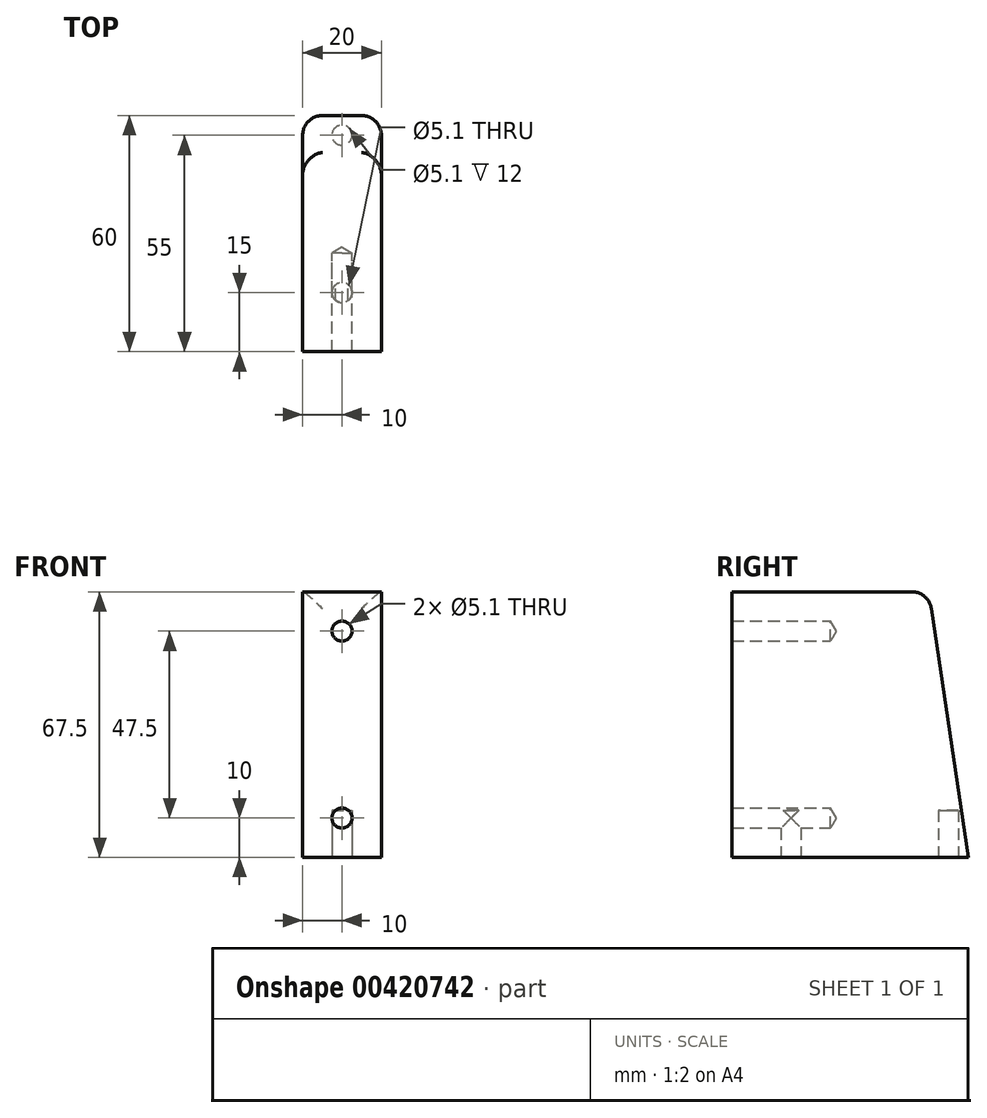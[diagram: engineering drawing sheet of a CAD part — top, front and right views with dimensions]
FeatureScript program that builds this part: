
annotation { "Feature Type Name" : "Feature", "Feature Type Description" : "" }
export const myFeature = defineFeature(function(context is Context, id is Id, definition is map)
    precondition{}
    {
        {
            var Q0;
            Q0=qCreatedBy(makeId("Right.planeOp"),FACE);
            var sketch = newSketch(context, id + "F0", { "sketchPlane" : qUnion([Q0])});
            skLineSegment(sketch, "E0", {"start": v(0, 0) * mm, "end": v(-60, 0) * mm});
            skLineSegment(sketch, "E1", {"start": v(-60, 0) * mm, "end": v(-60, 67.5) * mm});
            skLineSegment(sketch, "E2", {"start": v(-60, 67.5) * mm, "end": v(-10, 67.5) * mm});
            skLineSegment(sketch, "E3", {"start": v(-10, 67.5) * mm, "end": v(0, 0) * mm});
            skSolve(sketch);
        }
        {
            var Q0;
            Q0=qSketchRegion(id+"F0",true);
            extrude(context, id + "F1", {"entities" : qUnion([Q0]), "depth" : 20 * mm});
        }
        {
            var Q0;
            Q0=makeQuery(id+"F1.opExtrude","SWEPT_FACE",FACE,{"disambiguationData":[OSD([sQuery(id+"F0.wireOp",EDGE,"E1")])]});
            var sketch = newSketch(context, id + "F2", { "sketchPlane" : qUnion([Q0])});
            skLineSegment(sketch, "E4", {"start": v(10, 67.5) * mm, "end": v(10, 57.5) * mm});
            skLineSegment(sketch, "E5", {"start": v(10, 0) * mm, "end": v(10, 10) * mm});
            skSolve(sketch);
        }
        {
            var Q0;
            Q0=sQuery(id+"F2.wireOp",VERTEX,"E4.end");
            var Q1;
            Q1=sQuery(id+"F2.wireOp",VERTEX,"E5.end");
            var Q2;
            Q2=makeQuery(id+"F1.opExtrude","SWEPT_BODY",BODY,{"disambiguationData":[OSD([sQuery(id+"F0.wireOp",EDGE,"E0"),sQuery(id+"F0.wireOp",EDGE,"E1"),sQuery(id+"F0.wireOp",EDGE,"E2"),sQuery(id+"F0.wireOp",EDGE,"E3")])]});
            hole(context, id + "F3", {"style" : HoleStyle.SIMPLE, "endStyle" : HoleEndStyle.BLIND, "holeDiameter" : 5.1 * mm, "holeDepth" : 25 * mm, "isTappedThrough" : true, "tappedDepth" : 12 * mm, "tapClearance" : 3, "locations" : qUnion([Q0, Q1]), "scope" : qUnion([Q2]), "startStyle" : HoleStartStyle.PART});
        }
        {
            var Q0;
            Q0=makeQuery(id+"F1.opExtrude","SWEPT_FACE",FACE,{"disambiguationData":[OSD([sQuery(id+"F0.wireOp",EDGE,"E0")])]});
            var sketch = newSketch(context, id + "F4", { "sketchPlane" : qUnion([Q0])});
            skLineSegment(sketch, "E6", {"start": v(10, 60) * mm, "end": v(10, 45) * mm});
            skLineSegment(sketch, "E7", {"start": v(10, 45) * mm, "end": v(10, 5) * mm});
            skPoint(sketch, "E7.endSnap0", {"position": v(10, 0) * mm});
            skCircle(sketch, "E8", {"center": v(10, 45) * mm, "radius": 2.55 * mm});
            skCircle(sketch, "E9", {"center": v(10, 5) * mm, "radius": 2.55 * mm});
            skSolve(sketch);
        }
        {
            var Q0;
            Q0=qSketchRegion(id+"F4",true);
            extrude(context, id + "F5", {"entities" : qUnion([Q0]), "operationType" : NewBodyOperationType.REMOVE, "oppositeDirection" : true, "depth" : 12 * mm});
        }
        {
            var Q0;
            Q0=makeQuery(id+"F1.opExtrude","SWEPT_EDGE",EDGE,{"disambiguationData":[OSD([sQuery(id+"F0.wireOp",EDGE,"E2"),sQuery(id+"F0.wireOp",EDGE,"E3")])]});
            var Q1;
            Q1=makeQuery(id+"F1.opExtrude","CAP_EDGE",EDGE,{"disambiguationData":[OSD([sQuery(id+"F0.wireOp",EDGE,"E3")])],"isStart":false});
            var Q2;
            Q2=makeQuery(id+"F1.opExtrude","CAP_EDGE",EDGE,{"disambiguationData":[OSD([sQuery(id+"F0.wireOp",EDGE,"E3")])],"isStart":true});
            fillet(context, id + "F6", {"entities" : qUnion([Q0, Q1, Q2]), "radius" : 5 * mm, "tangentPropagation" : true, "allowEdgeOverflow" : false});
        }
    });
